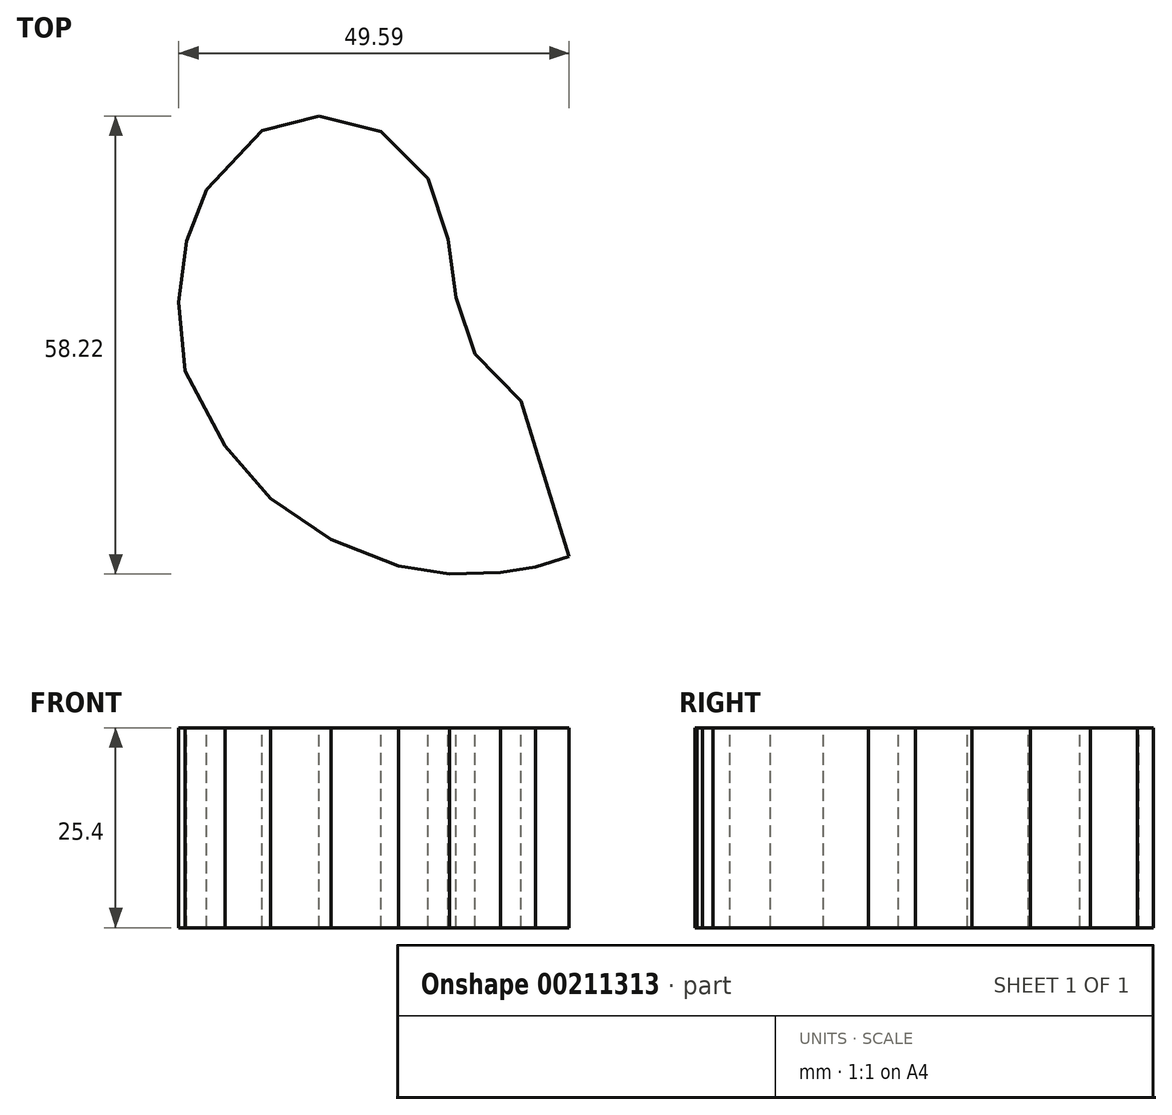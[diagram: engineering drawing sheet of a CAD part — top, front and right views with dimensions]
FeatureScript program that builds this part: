
annotation { "Feature Type Name" : "Feature", "Feature Type Description" : "" }
export const myFeature = defineFeature(function(context is Context, id is Id, definition is map)
    precondition{}
    {
        {
            var Q0;
            Q0=qCreatedBy(makeId("Top.planeOp"),FACE);
            var sketch = newSketch(context, id + "F0", { "sketchPlane" : qUnion([Q0])});
            skArc(sketch, "E0", {"start": v(-12.57, 6.93) * mm, "mid": v(-13.7, -4.25) * mm, "end": v(-6.45, -12.82) * mm});
            skFitSpline(sketch, "E1", {"points": [v(-12.57, 6.93) * mm, v(-18.39, 12.9) * mm, v(-20.8, 20.07) * mm, v(-21.86, 27.48) * mm, v(-24.36, 35.14) * mm, v(-30.32, 41.11) * mm, v(-38.22, 43.13) * mm, v(-45.48, 41.27) * mm, v(-52.5, 33.77) * mm, v(-55.08, 27.24) * mm, v(-56.04, 19.5) * mm, v(-55.24, 10.71) * mm, v(-50.16, 1.2) * mm, v(-44.35, -5.5) * mm, v(-36.7, -10.65) * mm, v(-28.15, -14.04) * mm, v(-21.62, -15.09) * mm, v(-15.16, -14.86) * mm, v(-10.74, -14.16) * mm, v(-6.45, -12.82) * mm], "startDerivative": vector(-151.34, 79.33) * mm, "endDerivative": vector(138.16, 43.75) * mm});
            skSolve(sketch);
        }
        {
            var Q0;
            Q0=qCreatedBy(makeId("Top.planeOp"),FACE);
            var sketch = newSketch(context, id + "F1", { "sketchPlane" : qUnion([Q0])});
            skPoint(sketch, "E2", {"position": v(-12.57, 6.93) * mm});
            skPoint(sketch, "E3.0", {"position": v(-18.39, 12.9) * mm});
            skPoint(sketch, "E4.0", {"position": v(-20.8, 20.07) * mm});
            skPoint(sketch, "E5.0", {"position": v(-21.86, 27.48) * mm});
            skPoint(sketch, "E6.0", {"position": v(-24.36, 35.14) * mm});
            skPoint(sketch, "E7.0", {"position": v(-30.32, 41.11) * mm});
            skPoint(sketch, "E8.0", {"position": v(-38.22, 43.13) * mm});
            skPoint(sketch, "E9.0", {"position": v(-45.48, 41.27) * mm});
            skPoint(sketch, "E10.0", {"position": v(-52.5, 33.77) * mm});
            skPoint(sketch, "E11.0", {"position": v(-55.08, 27.24) * mm});
            skPoint(sketch, "E12.0", {"position": v(-56.04, 19.5) * mm});
            skPoint(sketch, "E13.0", {"position": v(-55.24, 10.71) * mm});
            skPoint(sketch, "E14.0", {"position": v(-50.16, 1.2) * mm});
            skPoint(sketch, "E15.0", {"position": v(-44.35, -5.5) * mm});
            skPoint(sketch, "E16.0", {"position": v(-36.7, -10.65) * mm});
            skPoint(sketch, "E17.0", {"position": v(-28.15, -14.04) * mm});
            skPoint(sketch, "E18.0", {"position": v(-21.62, -15.09) * mm});
            skPoint(sketch, "E19.0", {"position": v(-15.16, -14.86) * mm});
            skPoint(sketch, "E20.0", {"position": v(-10.74, -14.16) * mm});
            skPoint(sketch, "E21.0", {"position": v(-6.45, -12.82) * mm});
            skLineSegment(sketch, "E22", {"start": v(-12.57, 6.93) * mm, "end": v(-18.39, 12.9) * mm});
            skLineSegment(sketch, "E23", {"start": v(-20.8, 20.07) * mm, "end": v(-18.39, 12.9) * mm});
            skLineSegment(sketch, "E24", {"start": v(-21.86, 27.48) * mm, "end": v(-20.8, 20.07) * mm});
            skLineSegment(sketch, "E25", {"start": v(-24.36, 35.14) * mm, "end": v(-21.86, 27.48) * mm});
            skLineSegment(sketch, "E26", {"start": v(-30.32, 41.11) * mm, "end": v(-24.36, 35.14) * mm});
            skLineSegment(sketch, "E27", {"start": v(-38.22, 43.13) * mm, "end": v(-30.32, 41.11) * mm});
            skLineSegment(sketch, "E28", {"start": v(-45.48, 41.27) * mm, "end": v(-38.22, 43.13) * mm});
            skLineSegment(sketch, "E29", {"start": v(-52.5, 33.77) * mm, "end": v(-45.48, 41.27) * mm});
            skLineSegment(sketch, "E30", {"start": v(-55.08, 27.24) * mm, "end": v(-52.5, 33.77) * mm});
            skLineSegment(sketch, "E31", {"start": v(-56.04, 19.5) * mm, "end": v(-55.08, 27.24) * mm});
            skLineSegment(sketch, "E32", {"start": v(-55.24, 10.71) * mm, "end": v(-56.04, 19.5) * mm});
            skLineSegment(sketch, "E33", {"start": v(-50.16, 1.2) * mm, "end": v(-55.24, 10.71) * mm});
            skLineSegment(sketch, "E34", {"start": v(-44.35, -5.5) * mm, "end": v(-50.16, 1.2) * mm});
            skLineSegment(sketch, "E35", {"start": v(-36.7, -10.65) * mm, "end": v(-44.35, -5.5) * mm});
            skLineSegment(sketch, "E36", {"start": v(-28.15, -14.04) * mm, "end": v(-36.7, -10.65) * mm});
            skLineSegment(sketch, "E37", {"start": v(-21.62, -15.09) * mm, "end": v(-28.15, -14.04) * mm});
            skLineSegment(sketch, "E38", {"start": v(-15.16, -14.86) * mm, "end": v(-21.62, -15.09) * mm});
            skLineSegment(sketch, "E39", {"start": v(-10.74, -14.16) * mm, "end": v(-15.16, -14.86) * mm});
            skLineSegment(sketch, "E40", {"start": v(-6.45, -12.82) * mm, "end": v(-10.74, -14.16) * mm});
            skLineSegment(sketch, "E41", {"start": v(-6.45, -12.82) * mm, "end": v(-12.57, 6.93) * mm});
            skSolve(sketch);
        }
        {
            var Q0;
            Q0=sQuery(id+"F1.wireOp",EDGE,"E40");
            var Q1;
            Q1=sQuery(id+"F1.wireOp",EDGE,"E34");
            var Q2;
            Q2=sQuery(id+"F1.wireOp",EDGE,"E31");
            var Q3;
            Q3=sQuery(id+"F1.wireOp",EDGE,"E30");
            var Q4;
            Q4=sQuery(id+"F1.wireOp",EDGE,"E32");
            var Q5;
            Q5=sQuery(id+"F1.wireOp",EDGE,"E29");
            var Q6;
            Q6=sQuery(id+"F1.wireOp",EDGE,"E41");
            var Q7;
            Q7=sQuery(id+"F1.wireOp",EDGE,"E33");
            var Q8;
            Q8=sQuery(id+"F1.wireOp",EDGE,"E28");
            var Q9;
            Q9=sQuery(id+"F1.wireOp",EDGE,"E36");
            var Q10;
            Q10=sQuery(id+"F1.wireOp",EDGE,"E27");
            var Q11;
            Q11=sQuery(id+"F1.wireOp",EDGE,"E39");
            var Q12;
            Q12=sQuery(id+"F1.wireOp",EDGE,"E24");
            var Q13;
            Q13=sQuery(id+"F1.wireOp",EDGE,"E35");
            var Q14;
            Q14=sQuery(id+"F1.wireOp",EDGE,"E23");
            var Q15;
            Q15=sQuery(id+"F1.wireOp",EDGE,"E22");
            var Q16;
            Q16=sQuery(id+"F1.wireOp",EDGE,"E37");
            var Q17;
            Q17=sQuery(id+"F1.wireOp",EDGE,"E38");
            var Q18;
            Q18=sQuery(id+"F1.wireOp",EDGE,"E25");
            var Q19;
            Q19=sQuery(id+"F1.wireOp",EDGE,"E26");
            extrude(context, id + "F2", {"bodyType" : ToolBodyType.SURFACE, "surfaceEntities" : qUnion([Q0, Q1, Q2, Q3, Q4, Q5, Q6, Q7, Q8, Q9, Q10, Q11, Q12, Q13, Q14, Q15, Q16, Q17, Q18, Q19]), "depth" : 25.4 * mm});
        }
    });
